# Revit family: Grease_Interceptor-Jay R Smith-P500-CSA_Series
name_source: partatom
category: Specialty Equipment
revit_build: Autodesk Revit 2014 (Build: 20130308_1515(x64)
units: mm (PartAtom-declared; Revit-internal decimal feet)

## types (11) — shared parameters
Assembly Code = D2090300
Description = Grease Interceptor
G (Plug Size) = 1.5 "
Manufacturer = Jay R Smith
Material = Steel Coal Tar-Jay R Smith-Epoxy Coated
Price = Prices may vary. Please consult Manufacturer Representative for most up-to-date price list.
Product Documentation Link = https://www.jrsmith.com
URL = https://www.jrsmith.com

## per-type parameters (varying)
| type | A | B | C | D | E | F (Width) | GPM FLOW RATE (L/M) | GREASE CAP LBS (KG) |
| P500-004 | 2 " | 6.875 " | 2.75 " | 12.25 " | 9.625 " | 13 " | 4(15) | 8(3.6) |
| P500-007 | 2 " | 7.75 " | 3.25 " | 13.625 " | 11 " | 14.5 " | 7(26) | 14(6) |
| P500-010 | 2 " | 8.75 " | 3.625 " | 15 " | 12.375 " | 15.75 " | 10(38) | 20(9) |
| P500-015 | 2 " | 11.25 " | 3.5 " | 17.375 " | 14.75 " | 18.25 " | 15(57) | 30(13.6) |
| P500-020 | 3 " | 12.75 " | 4 " | 19.375 " | 16.75 " | 20.25 " | 20(75) | 40(18) |
| P500-025 | 3 " | 14.25 " | 4.125 " | 21 " | 18.375 " | 21.75 " | 25(95) | 50(22.6) |
| P500-035 | 3 " | 14.5 " | 4.5 " | 22.375 " | 19 " | 23.25 " | 35(132) | 70(32) |
| P500-050 | 3 " | 14.5 " | 5.25 " | 31.625 " | 19.75 " | 23.25 " | 50(189) | 100(45) |
| P500-L20 | 3 " | 7 " | 3.75 " | 39.5 " | 10.5 " | 20.75 " | 20(75) | 40(18) |
| P500-L35 | 3 " | 7 " | 4.75 " | 52.25 " | 11.75 " | 26.75 " | 35(132) | 70(32) |
| P500-L50 | 3 " | 10 " | 5.938 " | 50.25 " | 15.938 " | 26.75 " | 50(189) | 100(45) |

note: column(s) folded — value = type name in every type: Model

## geometry (parser evidence)
native form markers: Sweep x3
no freeform markers — native parametric forms only
